# Revit family: Lollygagger Alfresco Bench 58
name_source: partatom
category: Furniture
revit_build: Autodesk Revit 2016 (Build: 20150220_1215(x64)
units: mm (PartAtom-declared; Revit-internal decimal feet)

## family parameters
Always vertical = Yes
Cut with Voids When Loaded = No
OmniClass Number = 23.40.20.00
OmniClass Title = General Furniture and Specialties
Room Calculation Point = No
Shared = No
Work Plane-Based = No

## types (10) — shared parameters
Height = 17 23/32"
Length = 58"
Manufacturer = Loll
Thick = 5/8"
Type Image = alfresco_bench_58.jpg
URL = https://lolldesigns.com
Width = 14 3/4"

## per-type parameters (varying)
| type | Finish Material |
| Loll-Black | Loll-Driftwood |
| Loll-Sunset | Loll-Sunset |
| Loll-Chocolate | Loll-Chocolate |
| Loll-Sky | Loll-Sky |
| Loll-Apple | Loll-Apple |
| Loll-Leaf | Loll-Leaf |
| Loll-Charcoal | Loll-Charcoal |
| Loll-Navy Blue | Loll-Navy Blue |
| Loll-White | Loll-White |
| Loll-Driftwood | Loll-Driftwood |

## geometry (parser evidence)
native form markers: Sweep x3
no freeform markers — native parametric forms only
